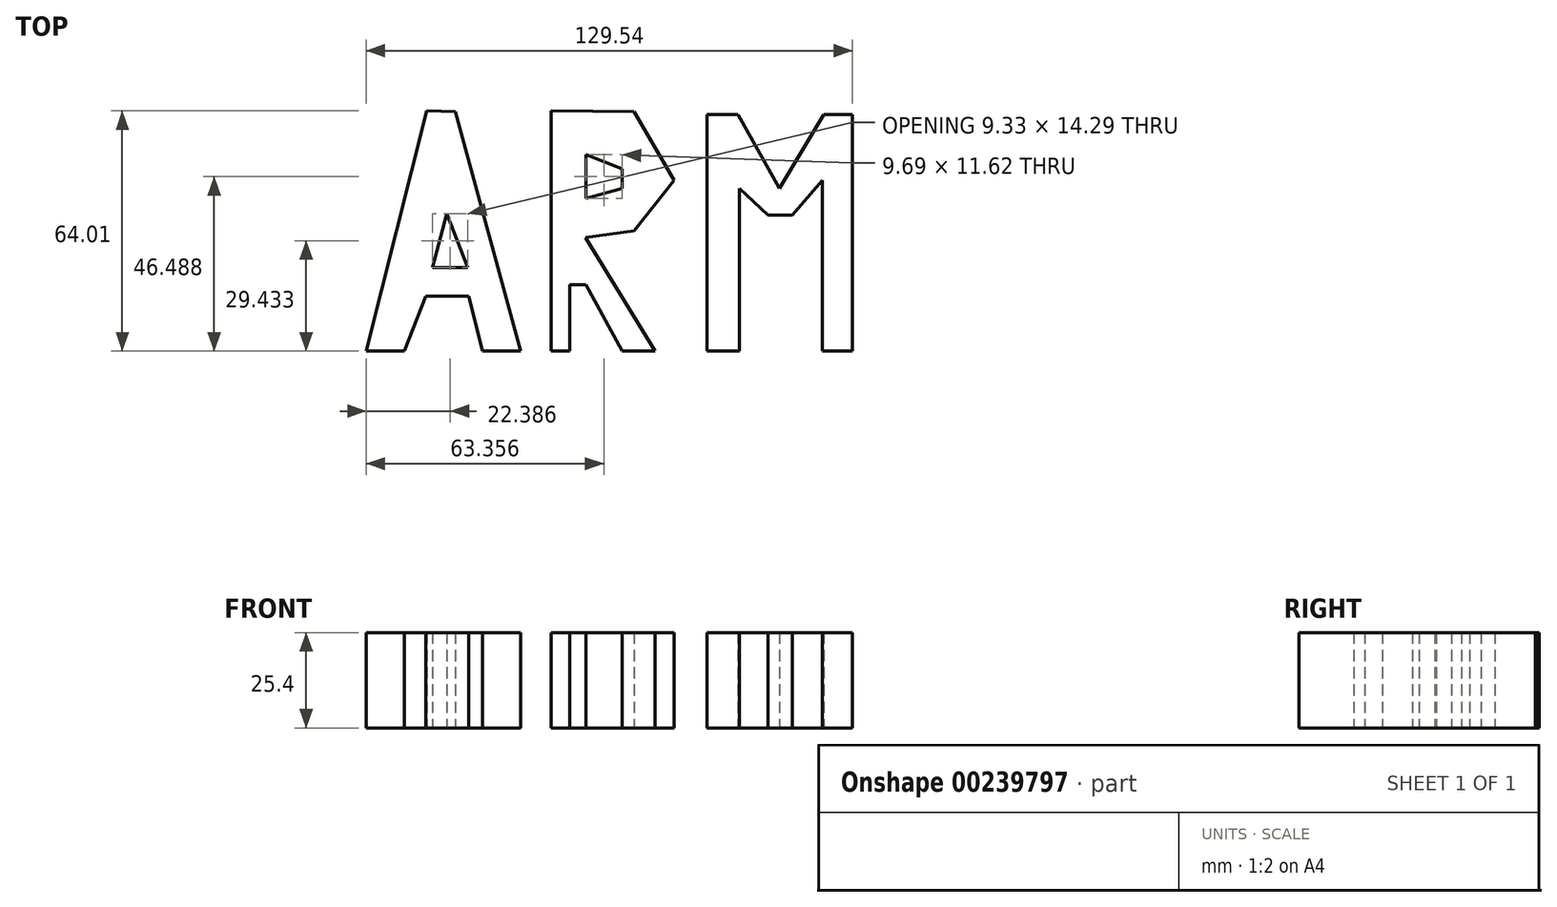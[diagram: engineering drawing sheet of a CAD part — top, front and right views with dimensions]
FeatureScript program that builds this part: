
annotation { "Feature Type Name" : "Feature", "Feature Type Description" : "" }
export const myFeature = defineFeature(function(context is Context, id is Id, definition is map)
    precondition{}
    {
        {
            var Q0;
            Q0=qCreatedBy(makeId("Top.planeOp"),FACE);
            var sketch = newSketch(context, id + "F0", { "sketchPlane" : qUnion([Q0])});
            skLineSegment(sketch, "E0", {"start": v(-55.25, 33.72) * mm, "end": v(-71.44, -30.29) * mm});
            skLineSegment(sketch, "E1", {"start": v(-71.44, -30.29) * mm, "end": v(-61.28, -30.29) * mm});
            skLineSegment(sketch, "E2", {"start": v(-61.28, -30.29) * mm, "end": v(-55.56, -15.62) * mm});
            skLineSegment(sketch, "E3", {"start": v(-55.56, -15.62) * mm, "end": v(-44.13, -15.62) * mm});
            skLineSegment(sketch, "E4", {"start": v(-44.13, -15.62) * mm, "end": v(-40.39, -30.29) * mm});
            skLineSegment(sketch, "E5", {"start": v(-40.39, -30.29) * mm, "end": v(-30.23, -30.29) * mm});
            skLineSegment(sketch, "E6", {"start": v(-30.23, -30.29) * mm, "end": v(-47.63, 33.53) * mm});
            skLineSegment(sketch, "E7", {"start": v(-47.63, 33.53) * mm, "end": v(-55.25, 33.72) * mm});
            skLineSegment(sketch, "E8", {"start": v(-22.1, -30.29) * mm, "end": v(-22.1, 33.72) * mm});
            skLineSegment(sketch, "E9", {"start": v(-22.1, 33.72) * mm, "end": v(0, 33.53) * mm});
            skLineSegment(sketch, "E10", {"start": v(0, 33.53) * mm, "end": v(10.67, 15.24) * mm});
            skLineSegment(sketch, "E11", {"start": v(10.67, 15.24) * mm, "end": v(0, 1.71) * mm});
            skLineSegment(sketch, "E12", {"start": v(0, 1.71) * mm, "end": v(-12.95, 0) * mm});
            skLineSegment(sketch, "E13", {"start": v(-12.95, 0) * mm, "end": v(5.52, -30.29) * mm});
            skLineSegment(sketch, "E14", {"start": v(5.52, -30.29) * mm, "end": v(-3.24, -30.29) * mm});
            skLineSegment(sketch, "E15", {"start": v(-3.24, -30.29) * mm, "end": v(-12.93, -12.66) * mm});
            skLineSegment(sketch, "E16", {"start": v(-12.93, -12.66) * mm, "end": v(-17.15, -12.66) * mm});
            skLineSegment(sketch, "E17", {"start": v(-17.15, -12.66) * mm, "end": v(-17.15, -30.29) * mm});
            skLineSegment(sketch, "E18", {"start": v(-17.15, -30.29) * mm, "end": v(-22.1, -30.29) * mm});
            skLineSegment(sketch, "E19", {"start": v(-12.93, 22) * mm, "end": v(-12.93, 10.39) * mm});
            skLineSegment(sketch, "E20", {"start": v(-12.93, 10.39) * mm, "end": v(-3.24, 13.03) * mm});
            skLineSegment(sketch, "E21", {"start": v(-3.24, 13.03) * mm, "end": v(-3.24, 18.29) * mm});
            skLineSegment(sketch, "E22", {"start": v(-3.24, 18.29) * mm, "end": v(-12.93, 22) * mm});
            skLineSegment(sketch, "E23", {"start": v(-53.72, -8) * mm, "end": v(-44.39, -8) * mm});
            skLineSegment(sketch, "E24", {"start": v(-44.39, -8) * mm, "end": v(-49.91, 6.29) * mm});
            skLineSegment(sketch, "E25", {"start": v(-49.91, 6.29) * mm, "end": v(-53.72, -8) * mm});
            skLineSegment(sketch, "E26", {"start": v(19.43, -30.29) * mm, "end": v(19.43, 32.77) * mm});
            skLineSegment(sketch, "E27", {"start": v(19.43, 32.77) * mm, "end": v(27.62, 32.77) * mm});
            skLineSegment(sketch, "E28", {"start": v(27.62, 32.77) * mm, "end": v(38.67, 13.03) * mm});
            skLineSegment(sketch, "E29", {"start": v(38.67, 13.03) * mm, "end": v(50.48, 32.77) * mm});
            skLineSegment(sketch, "E30", {"start": v(50.48, 32.77) * mm, "end": v(58.1, 32.77) * mm});
            skLineSegment(sketch, "E31", {"start": v(58.1, 32.77) * mm, "end": v(58.1, -30.29) * mm});
            skLineSegment(sketch, "E32", {"start": v(58.1, -30.29) * mm, "end": v(50.1, -30.29) * mm});
            skLineSegment(sketch, "E33", {"start": v(50.1, -30.29) * mm, "end": v(50.1, 15.24) * mm});
            skLineSegment(sketch, "E34", {"start": v(50.1, 15.24) * mm, "end": v(42.1, 5.9) * mm});
            skLineSegment(sketch, "E35", {"start": v(42.1, 5.9) * mm, "end": v(35.62, 5.9) * mm});
            skLineSegment(sketch, "E36", {"start": v(35.62, 5.9) * mm, "end": v(28, 13.03) * mm});
            skLineSegment(sketch, "E37", {"start": v(28, 13.03) * mm, "end": v(28, -30.29) * mm});
            skLineSegment(sketch, "E38", {"start": v(28, -30.29) * mm, "end": v(19.43, -30.29) * mm});
            skSolve(sketch);
        }
        {
            var Q0;
            Q0=makeQuery(id+"F0.imprint","IMPRINT",FACE,{"disambiguationData":[TD([[makeQuery(id+"F0.imprint","IMPRINT",EDGE,{"derivedFrom":sQuery(id+"F0.wireOp",EDGE,"E0")}),1.0]])]});
            var Q1;
            Q1=makeQuery(id+"F0.imprint","IMPRINT",FACE,{"disambiguationData":[TD([[makeQuery(id+"F0.imprint","IMPRINT",EDGE,{"derivedFrom":sQuery(id+"F0.wireOp",EDGE,"E8")}),-1.0]])]});
            var Q2;
            Q2=makeQuery(id+"F0.imprint","IMPRINT",FACE,{"disambiguationData":[TD([[makeQuery(id+"F0.imprint","IMPRINT",EDGE,{"derivedFrom":sQuery(id+"F0.wireOp",EDGE,"E26")}),-1.0]])]});
            extrude(context, id + "F1", {"entities" : qUnion([Q0, Q1, Q2]), "depth" : 25.4 * mm});
        }
    });
